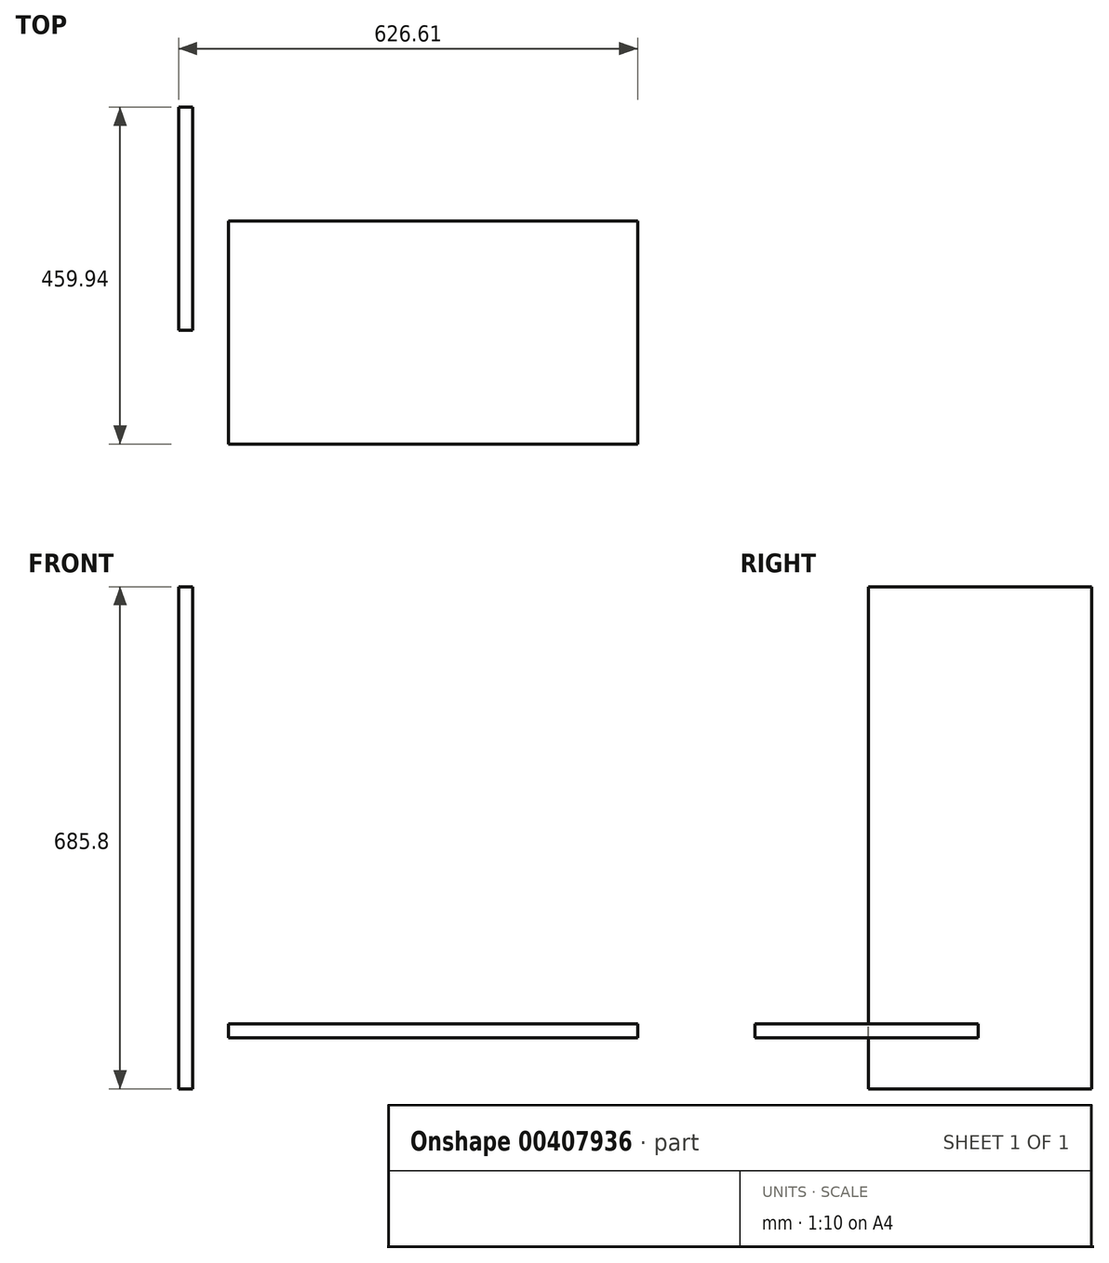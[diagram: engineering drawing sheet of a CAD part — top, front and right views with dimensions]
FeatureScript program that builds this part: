
annotation { "Feature Type Name" : "Feature", "Feature Type Description" : "" }
export const myFeature = defineFeature(function(context is Context, id is Id, definition is map)
    precondition{}
    {
        {
            var Q0;
            Q0=qCreatedBy(makeId("Right.planeOp"),FACE);
            var sketch = newSketch(context, id + "F0", { "sketchPlane" : qUnion([Q0])});
            skLineSegment(sketch, "E0.bottom", {"start": v(-68.85, -69.8) * mm, "end": v(235.95, -69.8) * mm});
            skLineSegment(sketch, "E0.top", {"start": v(-68.85, 616) * mm, "end": v(235.95, 616) * mm});
            skLineSegment(sketch, "E0.left", {"start": v(-68.85, -69.8) * mm, "end": v(-68.85, 616) * mm});
            skLineSegment(sketch, "E0.right", {"start": v(235.95, -69.8) * mm, "end": v(235.95, 616) * mm});
            skSolve(sketch);
        }
        {
            var Q0;
            Q0=makeQuery(id+"F0.imprint","IMPRINT",FACE,{"disambiguationData":[TD([[makeQuery(id+"F0.imprint","IMPRINT",EDGE,{"derivedFrom":sQuery(id+"F0.wireOp",EDGE,"E0.bottom")}),1.0]])]});
            extrude(context, id + "F1", {"entities" : qUnion([Q0]), "depth" : 19.05 * mm});
        }
        {
            var Q0;
            Q0=qCreatedBy(makeId("Top.planeOp"),FACE);
            var sketch = newSketch(context, id + "F2", { "sketchPlane" : qUnion([Q0])});
            skLineSegment(sketch, "E1.bottom", {"start": v(67.81, 80.81) * mm, "end": v(626.61, 80.81) * mm});
            skLineSegment(sketch, "E1.top", {"start": v(67.81, -223.99) * mm, "end": v(626.61, -223.99) * mm});
            skLineSegment(sketch, "E1.left", {"start": v(67.81, 80.81) * mm, "end": v(67.81, -223.99) * mm});
            skLineSegment(sketch, "E1.right", {"start": v(626.61, 80.81) * mm, "end": v(626.61, -223.99) * mm});
            skSolve(sketch);
        }
        {
            var Q0;
            Q0 = qSketchRegion(id + "F2", true);
            extrude(context, id + "F3", {"entities" : qUnion([Q0]), "depth" : 19.05 * mm});
        }
    });
